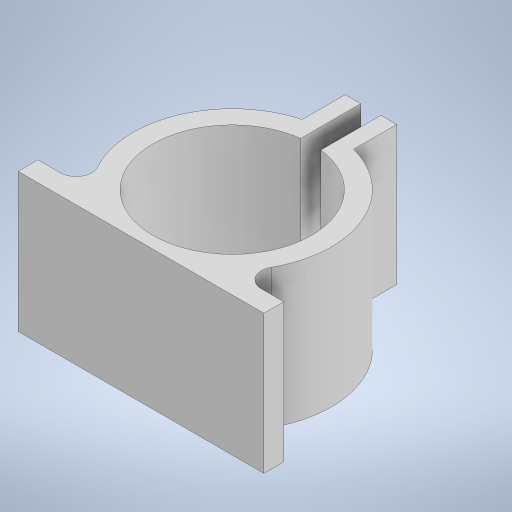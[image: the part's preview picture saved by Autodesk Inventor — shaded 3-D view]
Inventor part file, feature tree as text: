
AUTODESK INVENTOR PART (.ipt)
format: ipt  version: 2024 (Build 280153000, 153)  size: 344,064 bytes
history: native  units: mm
features: sketch x11, extrude x10, projected_geometry x4, fillet x1
ambient origin geometry x8: Origin, YZ Plane, XZ Plane, XY Plane, X Axis, Y Axis, Z Axis, Center Point
bodies: Solid1 (feature_tree)
feature tree (26):
  extrude  "Extrusion1"  Depth=70.0mm TaperAngle=0.0deg
  extrude  "Extrusion2"  TaperAngle=0.0deg  [1 undecoded]
  extrude  "Extrusion3"  Depth=6.0mm
  extrude  "Extrusion4"  Depth=70.0mm TaperAngle=0.0deg
  extrude  "Extrusion6"  Depth=70.0mm TaperAngle=0.0deg
  extrude  "Extrusion7"  Depth=70.0mm TaperAngle=0.0deg
  extrude  "Extrusion8"  [1 undecoded]
  extrude  "Extrusion9"  [1 undecoded]
  sketch  "Sketch10"
  fillet  "Fillet1"  [1 undecoded]
  extrude  "Extrusion10"  [1 undecoded]
  extrude  "Extrusion11"  [1 undecoded]
  sketch  "Sketch1"  dims[d0=100.0mm d1=70.0mm d2=0.0mm]
  sketch  "Sketch2"  dims[d3=100.0mm d4=0.0mm d5=0.0mm d6=0.0mm]
  sketch  "Sketch3"  dims[d7=6.0mm d8=0.0mm d9=6.1mm]
  sketch  "Sketch4"  dims[d12=70.0mm d13=0.0mm d14=70.0mm d15=0.0mm]
  sketch  "Sketch6"  dims[d16=10.0mm d17=0.0mm d18=70.0mm d19=0.0mm]
  sketch  "Sketch7"  dims[d20=8.0mm d21=70.0mm d22=0.0mm]
  sketch  "Sketch8"  dims[d23=70.0mm d24=0.0mm]
  projected_geometry  "Projected Loop2"
  projected_geometry  "Projected Loop3"
  sketch  "Sketch9"
  sketch  "Sketch11"
  sketch  "Sketch12"
  projected_geometry  "Projected Loop4"
  projected_geometry  "Projected Loop5"
note: 6 required parameter values undecoded (feature->parameter linkage not recoverable at this tier; creation-order binding heuristic only, values carry confidence <= 0.55)
